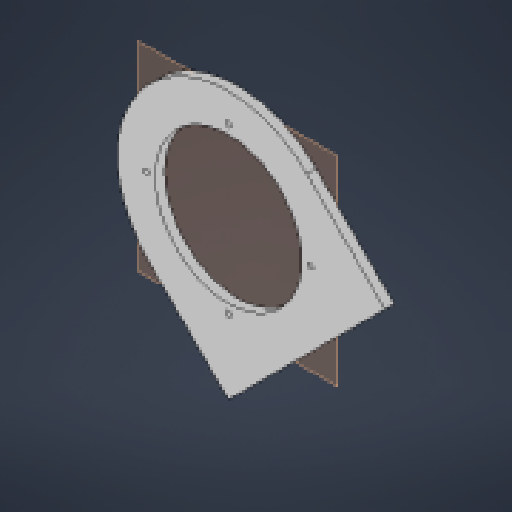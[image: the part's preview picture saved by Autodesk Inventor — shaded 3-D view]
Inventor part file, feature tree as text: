
AUTODESK INVENTOR PART (.ipt)
format: ipt  version: 2024 (Build 280153000, 153)  size: 136,704 bytes
history: native  units: in
note: dims shown in document units (in); Inventor stores cm internally (conversion verified against a paired STEP export)
features: other x3, plane x1, extrude x1, sketch x1, reference x1
ambient origin geometry x8: Origin, YZ Plane, XZ Plane, XY Plane, X Axis, Y Axis, Z Axis, Center Point
bodies: Solid1 (feature_tree)
feature tree (7):
  plane  "Work Plane1"
  extrude  "Extrusion1"  Depth=0.25in TaperAngle=0.0deg
  sketch  "Sketch1"  dims[d0=5.9055in d1=0.25in d2=0.0in]
  reference  "Reference1"
  other  "<userpath>\CodingProjects\C-AAM\CAD\V1\Parts\2ndAxis.iam"
  other  "2ndAxis.iam"
  other  "TopSpacer:1"
